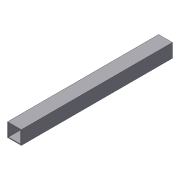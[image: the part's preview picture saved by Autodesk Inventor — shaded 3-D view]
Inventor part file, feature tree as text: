
AUTODESK INVENTOR PART (.ipt)
format: ipt  version: 2012 (Build 160160000, 160)  size: 72,192 bytes
history: native  units: in
note: dims shown in document units (in); Inventor stores cm internally (conversion verified against a paired STEP export)
features: extrude x1, shell x1, sketch x1
ambient origin geometry x8: Origin, YZ Plane, XZ Plane, XY Plane, X Axis, Y Axis, Z Axis, Center Point
bodies: Solid1 (feature_tree)
feature tree (3):
  extrude  "Extrusion1"  Depth=1.0in
  shell  "Shell1"  Thickness=11.0in
  sketch  "Sketch1"  dims[d0=1.0in d1=1.0in d2=11.0in d3=0.0in d4=0.0625in]
